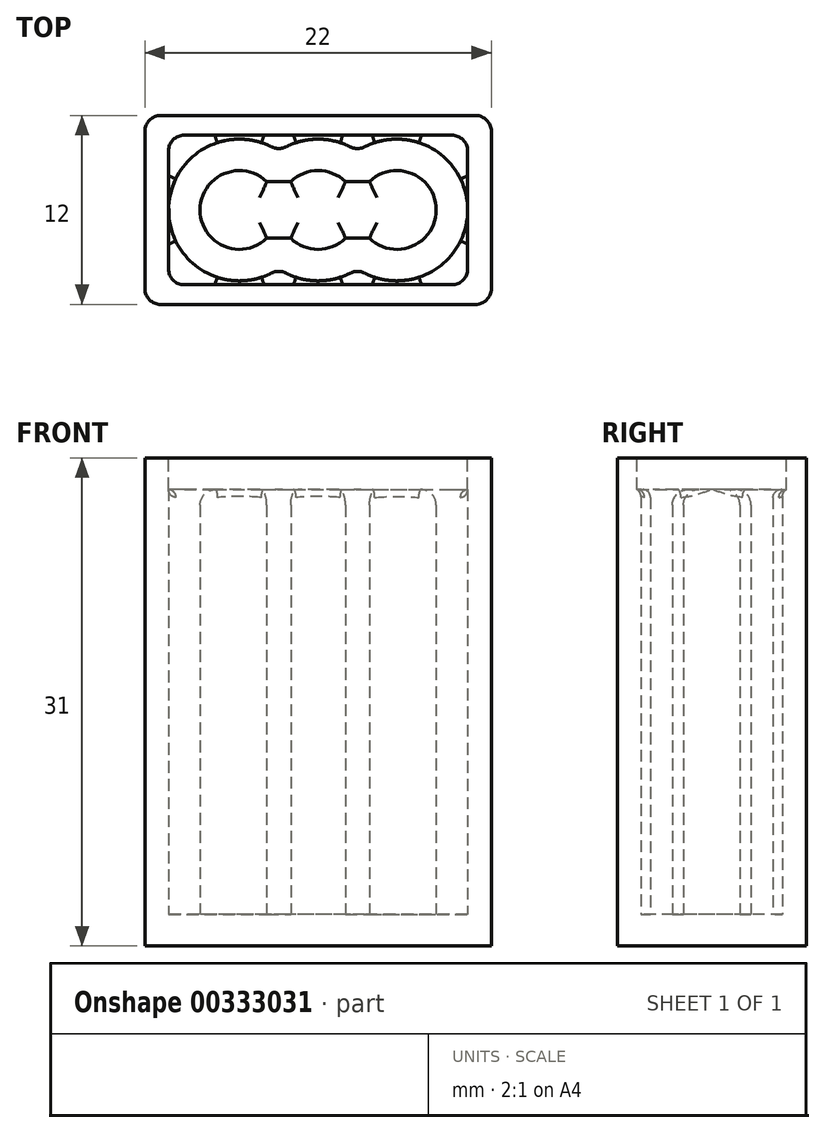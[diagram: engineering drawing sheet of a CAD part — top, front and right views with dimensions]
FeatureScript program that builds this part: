
annotation { "Feature Type Name" : "Feature", "Feature Type Description" : "" }
export const myFeature = defineFeature(function(context is Context, id is Id, definition is map)
    precondition{}
    {
        {
            var Q0;
            Q0=qCreatedBy(makeId("Top.planeOp"),FACE);
            var sketch = newSketch(context, id + "F0", { "sketchPlane" : qUnion([Q0])});
            skArc(sketch, "E0", {"start": v(-1.73, -1.8) * mm, "mid": v(0, -2.5) * mm, "end": v(1.73, -1.8) * mm});
            skArc(sketch, "E1", {"start": v(3.27, -1.8) * mm, "mid": v(7.5, 0) * mm, "end": v(3.27, 1.8) * mm});
            skArc(sketch, "E2", {"start": v(-3.27, 1.8) * mm, "mid": v(-7.5, 0) * mm, "end": v(-3.27, -1.8) * mm});
            skLineSegment(sketch, "E3", {"start": v(-3.27, -1.8) * mm, "end": v(-1.73, -1.8) * mm});
            skLineSegment(sketch, "E4", {"start": v(1.73, -1.8) * mm, "end": v(3.27, -1.8) * mm});
            skLineSegment(sketch, "E5", {"start": v(-3.27, 1.8) * mm, "end": v(-1.73, 1.8) * mm});
            skLineSegment(sketch, "E6", {"start": v(1.73, 1.8) * mm, "end": v(3.27, 1.8) * mm});
            skArc(sketch, "E7.trimOffspring", {"start": v(1.73, 1.8) * mm, "mid": v(0, 2.5) * mm, "end": v(-1.73, 1.8) * mm});
            skSolve(sketch);
        }
        {
            var Q0;
            Q0 = qSketchRegion(id + "F0", true);
            extrude(context, id + "F1", {"entities" : qUnion([Q0]), "depth" : 27 * mm});
        }
        {
            var Q0;
            Q0=makeQuery(id+"F1.opExtrude","CAP_FACE",FACE,{"disambiguationData":[OSD([sQuery(id+"F0.wireOp",EDGE,"E0")])],"isStart":true});
            var sketch = newSketch(context, id + "F2", { "sketchPlane" : qUnion([Q0])});
            skLineSegment(sketch, "E8.bottom", {"start": v(-11, 6) * mm, "end": v(11, 6) * mm});
            skLineSegment(sketch, "E8.top", {"start": v(-11, -6) * mm, "end": v(11, -6) * mm});
            skLineSegment(sketch, "E8.left", {"start": v(-11, 6) * mm, "end": v(-11, -6) * mm});
            skLineSegment(sketch, "E8.right", {"start": v(11, 6) * mm, "end": v(11, -6) * mm});
            skPoint(sketch, "E8.middle", {"position": v(0, 0) * mm});
            skSolve(sketch);
        }
        {
            var Q0;
            Q0 = qSketchRegion(id + "F2", true);
            extrude(context, id + "F3", {"entities" : qUnion([Q0]), "operationType" : NewBodyOperationType.ADD, "depth" : 2 * mm});
        }
        {
            var Q0;
            Q0=makeQuery(id+"F3.opExtrude","CAP_FACE",FACE,{"disambiguationData":[OSD([sQuery(id+"F2.wireOp",EDGE,"E8.bottom"),sQuery(id+"F2.wireOp",EDGE,"E8.top"),sQuery(id+"F2.wireOp",EDGE,"E8.left"),sQuery(id+"F2.wireOp",EDGE,"E8.right")])],"isStart":true});
            var sketch = newSketch(context, id + "F4", { "sketchPlane" : qUnion([Q0])});
            skLineSegment(sketch, "E9.bottom", {"start": v(-11, 6) * mm, "end": v(11, 6) * mm});
            skLineSegment(sketch, "E9.top", {"start": v(-11, -6) * mm, "end": v(11, -6) * mm});
            skLineSegment(sketch, "E9.left", {"start": v(-11, 6) * mm, "end": v(-11, -6) * mm});
            skLineSegment(sketch, "E9.right", {"start": v(11, 6) * mm, "end": v(11, -6) * mm});
            skPoint(sketch, "E9.middle", {"position": v(0, 0) * mm});
            skLineSegment(sketch, "E10.bottom", {"start": v(-8.5, 3.5) * mm, "end": v(8.5, 3.5) * mm, "construction": true});
            skLineSegment(sketch, "E10.top", {"start": v(-8.5, -3.5) * mm, "end": v(8.5, -3.5) * mm, "construction": true});
            skLineSegment(sketch, "E10.left", {"start": v(-8.5, 3.5) * mm, "end": v(-8.5, -3.5) * mm, "construction": true});
            skLineSegment(sketch, "E10.right", {"start": v(8.5, 3.5) * mm, "end": v(8.5, -3.5) * mm, "construction": true});
            skArc(sketch, "E11.0", {"start": v(-2.5, 3.74) * mm, "mid": v(-9.5, 0) * mm, "end": v(-2.5, -3.74) * mm});
            skArc(sketch, "E12.0", {"start": v(2.5, 3.74) * mm, "mid": v(0, 4.5) * mm, "end": v(-2.5, 3.74) * mm});
            skCircle(sketch, "E13.0", {"center": v(-5, 0) * mm, "radius": 1.97 * mm});
            skArc(sketch, "E14.0", {"start": v(2.5, -3.74) * mm, "mid": v(9.5, 0) * mm, "end": v(2.5, 3.74) * mm});
            skArc(sketch, "E15.trimOffspring", {"start": v(-2.5, -3.74) * mm, "mid": v(0, -4.5) * mm, "end": v(2.5, -3.74) * mm});
            skSolve(sketch);
        }
        {
            var Q0;
            Q0 = qSketchRegion(id + "F4", true);
            extrude(context, id + "F5", {"entities" : qUnion([Q0]), "operationType" : NewBodyOperationType.ADD, "depth" : 29 * mm});
        }
        {
            var Q0;
            Q0=makeQuery(id+"F1.opExtrude","CAP_FACE",FACE,{"disambiguationData":[OSD([sQuery(id+"F0.wireOp",EDGE,"E2")])],"isStart":false});
            var Q1;
            Q1=makeQuery(id+"F1.opExtrude","CAP_FACE",FACE,{"disambiguationData":[OSD([sQuery(id+"F0.wireOp",EDGE,"E0")])],"isStart":false});
            var Q2;
            Q2=makeQuery(id+"F1.opExtrude","CAP_FACE",FACE,{"disambiguationData":[OSD([sQuery(id+"F0.wireOp",EDGE,"E1")])],"isStart":false});
            fillet(context, id + "F6", {"entities" : qUnion([Q0, Q1, Q2]), "radius" : 1 * mm, "tangentPropagation" : true, "allowEdgeOverflow" : false});
        }
        {
            var Q0;
            Q0=makeQuery(id+"F5.opExtrude","CAP_FACE",FACE,{"disambiguationData":[OSD([sQuery(id+"F4.wireOp",EDGE,"E9.bottom"),sQuery(id+"F4.wireOp",EDGE,"E9.top"),sQuery(id+"F4.wireOp",EDGE,"E9.left"),sQuery(id+"F4.wireOp",EDGE,"E9.right"),sQuery(id+"F4.wireOp",EDGE,"E11.0"),sQuery(id+"F4.wireOp",EDGE,"E12.0"),sQuery(id+"F4.wireOp",EDGE,"E14.0"),sQuery(id+"F4.wireOp",EDGE,"E15.trimOffspring")])],"isStart":false});
            var sketch = newSketch(context, id + "F7", { "sketchPlane" : qUnion([Q0])});
            skLineSegment(sketch, "E16.bottom", {"start": v(-9.5, 4.75) * mm, "end": v(9.5, 4.75) * mm});
            skLineSegment(sketch, "E16.top", {"start": v(-9.5, -4.75) * mm, "end": v(9.5, -4.75) * mm});
            skLineSegment(sketch, "E16.left", {"start": v(-9.5, 4.75) * mm, "end": v(-9.5, -4.75) * mm});
            skLineSegment(sketch, "E16.right", {"start": v(9.5, 4.75) * mm, "end": v(9.5, -4.75) * mm});
            skPoint(sketch, "E16.middle", {"position": v(0, 0) * mm});
            skSolve(sketch);
        }
        {
            var Q0;
            Q0 = qSketchRegion(id + "F7", true);
            extrude(context, id + "F8", {"entities" : qUnion([Q0]), "operationType" : NewBodyOperationType.REMOVE, "oppositeDirection" : true, "depth" : 2 * mm});
        }
        {
            var Q0;
            Q0=makeQuery(id+"F5.opExtrude","SWEPT_EDGE",EDGE,{"disambiguationData":[OSD([sQuery(id+"F4.wireOp",EDGE,"E11.0"),sQuery(id+"F4.wireOp",EDGE,"E15.trimOffspring")])]});
            var Q1;
            Q1=makeQuery(id+"F5.opExtrude","SWEPT_EDGE",EDGE,{"disambiguationData":[OSD([sQuery(id+"F4.wireOp",EDGE,"E14.0"),sQuery(id+"F4.wireOp",EDGE,"E15.trimOffspring")])]});
            var Q2;
            Q2=makeQuery(id+"F5.opExtrude","SWEPT_EDGE",EDGE,{"disambiguationData":[OSD([sQuery(id+"F4.wireOp",EDGE,"E12.0"),sQuery(id+"F4.wireOp",EDGE,"E14.0")])]});
            var Q3;
            Q3=makeQuery(id+"F5.opExtrude","SWEPT_EDGE",EDGE,{"disambiguationData":[OSD([sQuery(id+"F4.wireOp",EDGE,"E11.0"),sQuery(id+"F4.wireOp",EDGE,"E12.0")])]});
            var Q4;
            Q4=makeQuery(id+"F5.boolean.opBoolean","MERGE",EDGE,{"derivedFrom":[makeQuery(id+"F3.opExtrude","SWEPT_EDGE",EDGE,{"disambiguationData":[OSD([sQuery(id+"F2.wireOp",EDGE,"E8.bottom"),sQuery(id+"F2.wireOp",EDGE,"E8.left")])]}),makeQuery(id+"F5.opExtrude","SWEPT_EDGE",EDGE,{"disambiguationData":[OSD([sQuery(id+"F4.wireOp",EDGE,"E9.top"),sQuery(id+"F4.wireOp",EDGE,"E9.left")])]})]});
            var Q5;
            Q5=makeQuery(id+"F5.boolean.opBoolean","MERGE",EDGE,{"derivedFrom":[makeQuery(id+"F3.opExtrude","SWEPT_EDGE",EDGE,{"disambiguationData":[OSD([sQuery(id+"F2.wireOp",EDGE,"E8.bottom"),sQuery(id+"F2.wireOp",EDGE,"E8.right")])]}),makeQuery(id+"F5.opExtrude","SWEPT_EDGE",EDGE,{"disambiguationData":[OSD([sQuery(id+"F4.wireOp",EDGE,"E9.top"),sQuery(id+"F4.wireOp",EDGE,"E9.right")])]})]});
            var Q6;
            Q6=makeQuery(id+"F5.boolean.opBoolean","MERGE",EDGE,{"derivedFrom":[makeQuery(id+"F3.opExtrude","SWEPT_EDGE",EDGE,{"disambiguationData":[OSD([sQuery(id+"F2.wireOp",EDGE,"E8.top"),sQuery(id+"F2.wireOp",EDGE,"E8.right")])]}),makeQuery(id+"F5.opExtrude","SWEPT_EDGE",EDGE,{"disambiguationData":[OSD([sQuery(id+"F4.wireOp",EDGE,"E9.bottom"),sQuery(id+"F4.wireOp",EDGE,"E9.right")])]})]});
            var Q7;
            Q7=makeQuery(id+"F5.boolean.opBoolean","MERGE",EDGE,{"derivedFrom":[makeQuery(id+"F3.opExtrude","SWEPT_EDGE",EDGE,{"disambiguationData":[OSD([sQuery(id+"F2.wireOp",EDGE,"E8.top"),sQuery(id+"F2.wireOp",EDGE,"E8.left")])]}),makeQuery(id+"F5.opExtrude","SWEPT_EDGE",EDGE,{"disambiguationData":[OSD([sQuery(id+"F4.wireOp",EDGE,"E9.bottom"),sQuery(id+"F4.wireOp",EDGE,"E9.left")])]})]});
            var Q8;
            Q8=makeQuery(id+"F8.boolean.opBoolean","COPY",EDGE,{"derivedFrom":makeQuery(id+"F8.opExtrude","SWEPT_EDGE",EDGE,{"disambiguationData":[OSD([sQuery(id+"F7.wireOp",EDGE,"E16.bottom"),sQuery(id+"F7.wireOp",EDGE,"E16.left")])]})});
            var Q9;
            Q9=makeQuery(id+"F8.boolean.opBoolean","COPY",EDGE,{"derivedFrom":makeQuery(id+"F8.opExtrude","SWEPT_EDGE",EDGE,{"disambiguationData":[OSD([sQuery(id+"F7.wireOp",EDGE,"E16.bottom"),sQuery(id+"F7.wireOp",EDGE,"E16.right")])]})});
            var Q10;
            Q10=makeQuery(id+"F8.boolean.opBoolean","COPY",EDGE,{"derivedFrom":makeQuery(id+"F8.opExtrude","SWEPT_EDGE",EDGE,{"disambiguationData":[OSD([sQuery(id+"F7.wireOp",EDGE,"E16.top"),sQuery(id+"F7.wireOp",EDGE,"E16.right")])]})});
            var Q11;
            Q11=makeQuery(id+"F8.boolean.opBoolean","COPY",EDGE,{"derivedFrom":makeQuery(id+"F8.opExtrude","SWEPT_EDGE",EDGE,{"disambiguationData":[OSD([sQuery(id+"F7.wireOp",EDGE,"E16.top"),sQuery(id+"F7.wireOp",EDGE,"E16.left")])]})});
            fillet(context, id + "F9", {"entities" : qUnion([Q0, Q1, Q2, Q3, Q4, Q5, Q6, Q7, Q8, Q9, Q10, Q11]), "radius" : 1 * mm, "tangentPropagation" : true, "allowEdgeOverflow" : false});
        }
        {
            var Q0;
            Q0=makeQuery(id+"F8.boolean.opBoolean","INTERSECT",EDGE,{"derivedFrom":[makeQuery(id+"F5.opExtrude","SWEPT_FACE",FACE,{"disambiguationData":[OSD([sQuery(id+"F4.wireOp",EDGE,"E11.0")])]}),makeQuery(id+"F8.opExtrude","CAP_FACE",FACE,{"disambiguationData":[OSD([sQuery(id+"F7.wireOp",EDGE,"E16.bottom"),sQuery(id+"F7.wireOp",EDGE,"E16.top"),sQuery(id+"F7.wireOp",EDGE,"E16.left"),sQuery(id+"F7.wireOp",EDGE,"E16.right")])],"isStart":false})]});
            fillet(context, id + "F10", {"entities" : qUnion([Q0]), "radius" : .5 * mm, "tangentPropagation" : true, "allowEdgeOverflow" : false});
        }
    });
